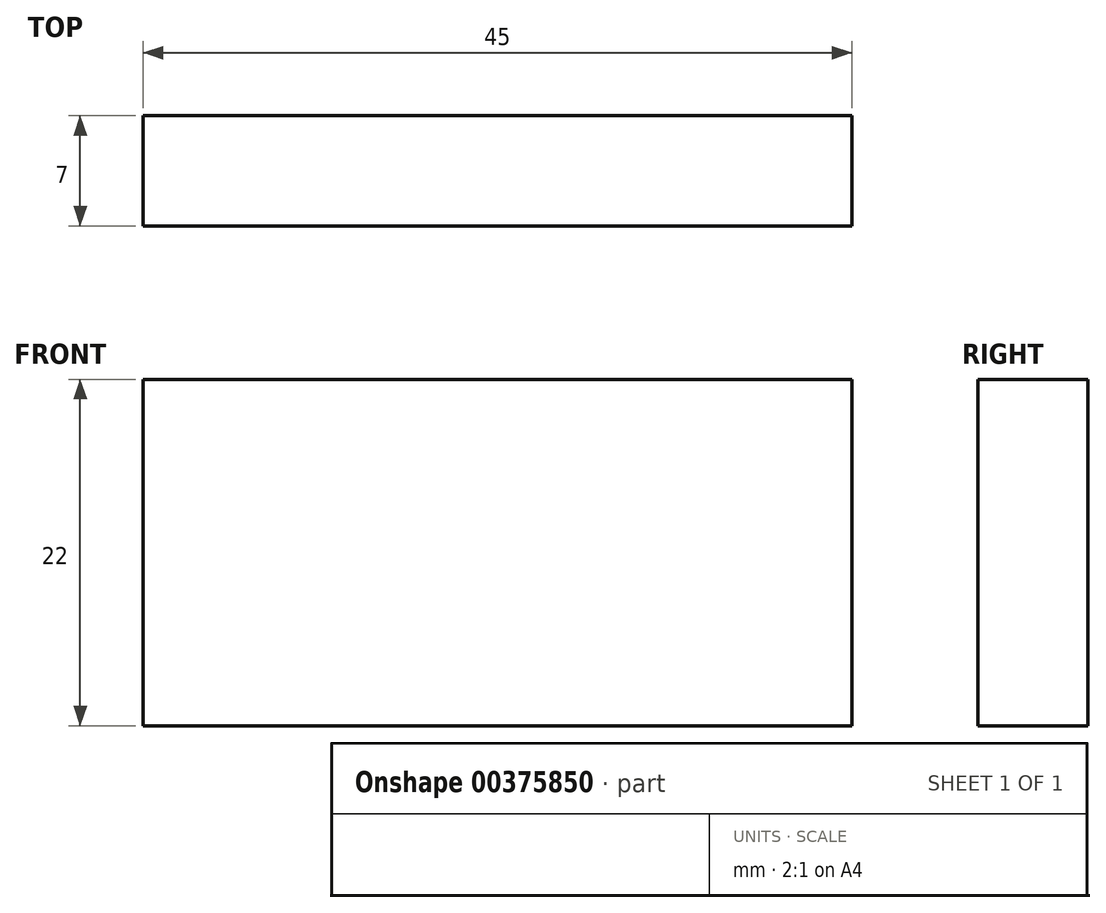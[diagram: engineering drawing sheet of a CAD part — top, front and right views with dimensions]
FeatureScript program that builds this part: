
annotation { "Feature Type Name" : "Feature", "Feature Type Description" : "" }
export const myFeature = defineFeature(function(context is Context, id is Id, definition is map)
    precondition{}
    {
        {
            var Q0;
            Q0=qCreatedBy(makeId("Front.planeOp"),FACE);
            var sketch = newSketch(context, id + "F0", { "sketchPlane" : qUnion([Q0])});
            skLineSegment(sketch, "E0.bottom", {"start": v(22.5, 11) * mm, "end": v(-22.5, 11) * mm});
            skLineSegment(sketch, "E0.top", {"start": v(22.5, -11) * mm, "end": v(-22.5, -11) * mm});
            skLineSegment(sketch, "E0.left", {"start": v(22.5, 11) * mm, "end": v(22.5, -11) * mm});
            skLineSegment(sketch, "E0.right", {"start": v(-22.5, 11) * mm, "end": v(-22.5, -11) * mm});
            skPoint(sketch, "E0.middle", {"position": v(0, 0) * mm});
            skSolve(sketch);
        }
        {
            var Q0;
            Q0 = qSketchRegion(id + "F0", true);
            extrude(context, id + "F1", {"entities" : qUnion([Q0]), "depth" : 7 * mm, "symmetric" : true});
        }
    });
